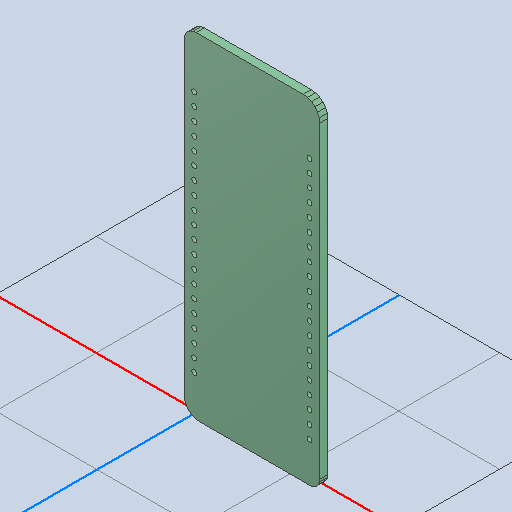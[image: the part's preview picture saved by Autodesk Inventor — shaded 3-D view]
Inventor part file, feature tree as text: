
AUTODESK INVENTOR PART (.ipt)
format: ipt  version: 2022 (Build 260153000, 153)  size: 257,536 bytes
history: native  units: mm
features: extrude x2, sketch x2, other x1
ambient origin geometry x8: Origin, YZ Plane, XZ Plane, XY Plane, X Axis, Y Axis, Z Axis, Center Point
bodies: Body1 (feature_tree)
feature tree (5):
  other  "Твердое тело1"
  extrude  "untitled.brdКонтур"  Depth=1.6mm TaperAngle=0.0deg
  extrude  "Выдавливание2"  Depth=30.75mm TaperAngle=0.0deg
  sketch  "Эскиз1"
  sketch  "Эскиз2"
